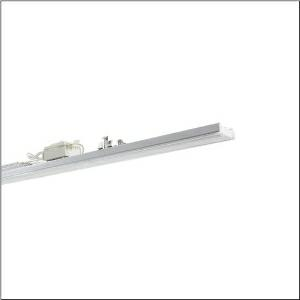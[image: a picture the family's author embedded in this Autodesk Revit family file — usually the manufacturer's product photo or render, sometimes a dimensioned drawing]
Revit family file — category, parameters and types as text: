
# Revit family: licross_11_recessed_mo_51tl14dn49xg
name_source: partatom
category: Lighting Fixtures
units: mm (PartAtom-declared; Revit-internal decimal feet)

## family parameters
Cut with Voids When Loaded = No
Host = Face
Light Source = No
Part Type = Normal
Room Calculation Point = No
Round Connector Dimension = Use Diameter
Shared = No

## types (1)
- --- (1 x LED, 9430 lm, 56.7 W, 4000K)
    Apparent Load = 57 VA
    CIE Flux Codes = 56 84 97 100 100
    Color Rendering = 80
    Color Temperature = 4000K
    Default Elevation = 1800 mm
    Description = Licross 11 Recessed MO, luminaire insert, of sheet steel, coil coated, white, length: 1.500mm, width: 66mm, height: 67mm, LED rated luminous flux: 9.430lm, light colour: 840, SDCM (Standard Deviation of Colour Matching)MacAdam ≤ 2 SDCM (initial), control gear: DALI 2, with plug, 5-pole, with phase selection, mains connection: 220..240V, AC, 50/60Hz, rated input power: 57W, internal wiring halogen-free, primary light control with lens, of plastic, primary optical cover: cover, of PMMA, light emission: direct distribution, primary light characteristic: asymmetric, protection rating (complete): IP40, insulation class (complete): insulation class I (protective earthing), certification: CE, ENEC, VDE, UKCA, protection symbol: D if used in an environment without relevant dust loads with corresponding accessories, impact resistance: IK06, permissible ambient temperature for indoor applications: -25..+35°C, corresponds to IFS (International Featured Standards) requirements for safety and quality in the food industry, reducing of maximum allowable ambient temperature of 5°C with ceiling mounting, LABS conformity tested according to VDMA 24364:2018-05, The light source and the operating device comply with the requirements of the Ecodesign Regulation (EU) 2019/2020 and are replaceable in accordance with this regulation, packaging unit: 1 piece
    Height = 58 mm
    Lamp = 1 x LED
    Lamp Light Flux = 9430 lm
    Lamp Power = 56.7 W
    Lamp count = 1
    Length = 1500 mm
    Luminous efficacy = 166 lm/W
    Manufacturer = Siteco
    ModVariant = No
    Model = 51TL14DN49XG
    Mounting Place = Ceiling
    Mounting Type = Pendant
    Number of Poles = 1
    OnlyDefault = Yes
    Power Factor = 1
    Product Name = Licross 11 Recessed MO
    Product group = luminaire insert | ceiling pendant
    ProductGroupID = 901
    Protection Class = Protection class I
    Protection Degree = IP 40
    RLX_Detail_Level = 1
    RLX_Emergency_Light_Flux = 0 lm
    RLX_Emergency_Type = 0
    RLX_Emergency_Type_DB = No
    RlxData = <blob elided: 25161 chars, md5=3909b925>
    Socket = socket
    Standby Power = 0 W
    System Light Flux = 9430 lm
    System Power = 57 W
    Type Comments = factory setting: luminous flux: 100 % | dim-lin: 254 | 378 mA
    Type Image = l_1296930.jpg
    URL = http://relux.com
    VarID = @adj_101647
    Voltage = 0 V
    Weight = 0.00 kg
    Width = 66 mm

## geometry (parser evidence)
native form markers: Blend x4, Sweep x11
no freeform markers — native parametric forms only
